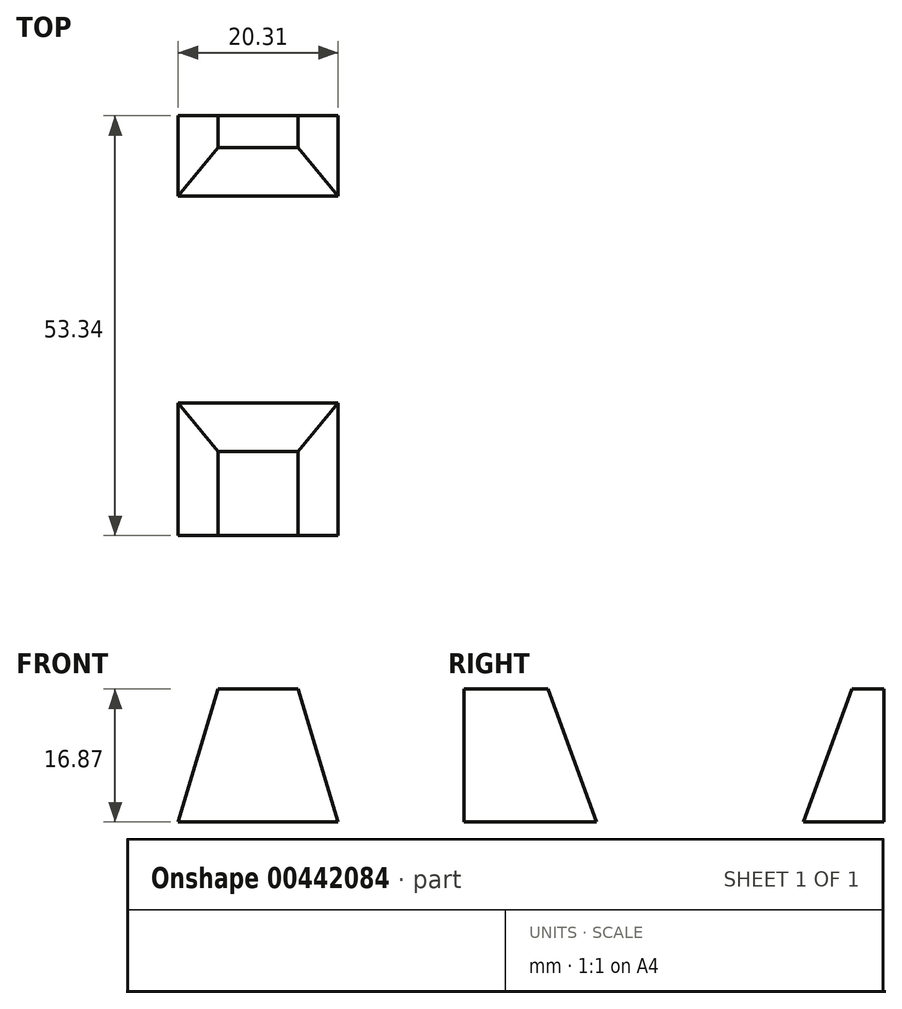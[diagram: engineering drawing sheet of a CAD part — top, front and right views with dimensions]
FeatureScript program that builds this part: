
annotation { "Feature Type Name" : "Feature", "Feature Type Description" : "" }
export const myFeature = defineFeature(function(context is Context, id is Id, definition is map)
    precondition{}
    {
        {
            var Q0;
            Q0=qCreatedBy(makeId("Front.planeOp"),FACE);
            var sketch = newSketch(context, id + "F0", { "sketchPlane" : qUnion([Q0])});
            skLineSegment(sketch, "E0", {"start": v(0, 0) * mm, "end": v(0, 8.53) * mm});
            skLineSegment(sketch, "E1", {"start": v(0, 8.53) * mm, "end": v(0, -8.34) * mm});
            skLineSegment(sketch, "E2", {"start": v(0, -8.34) * mm, "end": v(-10.16, -8.34) * mm});
            skLineSegment(sketch, "E3", {"start": v(-10.16, -8.34) * mm, "end": v(10.15, -8.34) * mm});
            skPoint(sketch, "E3.endSnap0", {"position": v(-5.08, -8.34) * mm});
            skLineSegment(sketch, "E4", {"start": v(0, 8.53) * mm, "end": v(5.07, 8.53) * mm});
            skLineSegment(sketch, "E5", {"start": v(5.07, 8.53) * mm, "end": v(10.15, -8.34) * mm});
            skLineSegment(sketch, "E6", {"start": v(0, 8.53) * mm, "end": v(-5.07, 8.53) * mm});
            skLineSegment(sketch, "E7", {"start": v(-5.07, 8.53) * mm, "end": v(-10.16, -8.34) * mm});
            skSolve(sketch);
        }
        {
            var Q0;
            Q0 = qSketchRegion(id + "F0", true);
            extrude(context, id + "F1", {"entities" : qUnion([Q0]), "depth" : 23.37 * mm});
        }
        {
            var Q0;
            Q0=makeQuery(id+"F1.opExtrude","CAP_EDGE",EDGE,{"disambiguationData":[OSD([sQuery(id+"F0.wireOp",EDGE,"E4"),sQuery(id+"F0.wireOp",EDGE,"E6")])],"isStart":true});
            chamfer(context, id + "F2", {"entities" : qUnion([Q0]), "chamferType" : ChamferType.OFFSET_ANGLE, "width" : 19.3 * mm, "oppositeDirection" : false, "angle" : 70 * degree});
        }
        {
            var Q0;
            Q0=makeQuery(id+"F1.opExtrude","SWEPT_BODY",BODY,{"disambiguationData":[OSD([sQuery(id+"F0.wireOp",EDGE,"E3"),sQuery(id+"F0.wireOp",EDGE,"E4"),sQuery(id+"F0.wireOp",EDGE,"E5"),sQuery(id+"F0.wireOp",EDGE,"E6"),sQuery(id+"F0.wireOp",EDGE,"E7")])]});
            var Q1;
            Q1=qCreatedBy(makeId("Front.planeOp"),FACE);
            mirror(context, id + "F3", {"entities" : qUnion([Q0]), "mirrorPlane" : qUnion([Q1])});
        }
        {
            var Q0;
            Q0=makeQuery(id+"F1.opExtrude","CAP_FACE",FACE,{"disambiguationData":[OSD([sQuery(id+"F0.wireOp",EDGE,"E3"),sQuery(id+"F0.wireOp",EDGE,"E4"),sQuery(id+"F0.wireOp",EDGE,"E5"),sQuery(id+"F0.wireOp",EDGE,"E6"),sQuery(id+"F0.wireOp",EDGE,"E7")])],"isStart":false});
            extrude(context, id + "F4", {"entities" : qUnion([Q0]), "operationType" : NewBodyOperationType.ADD, "depth" : 6.6 * mm});
        }
    });
